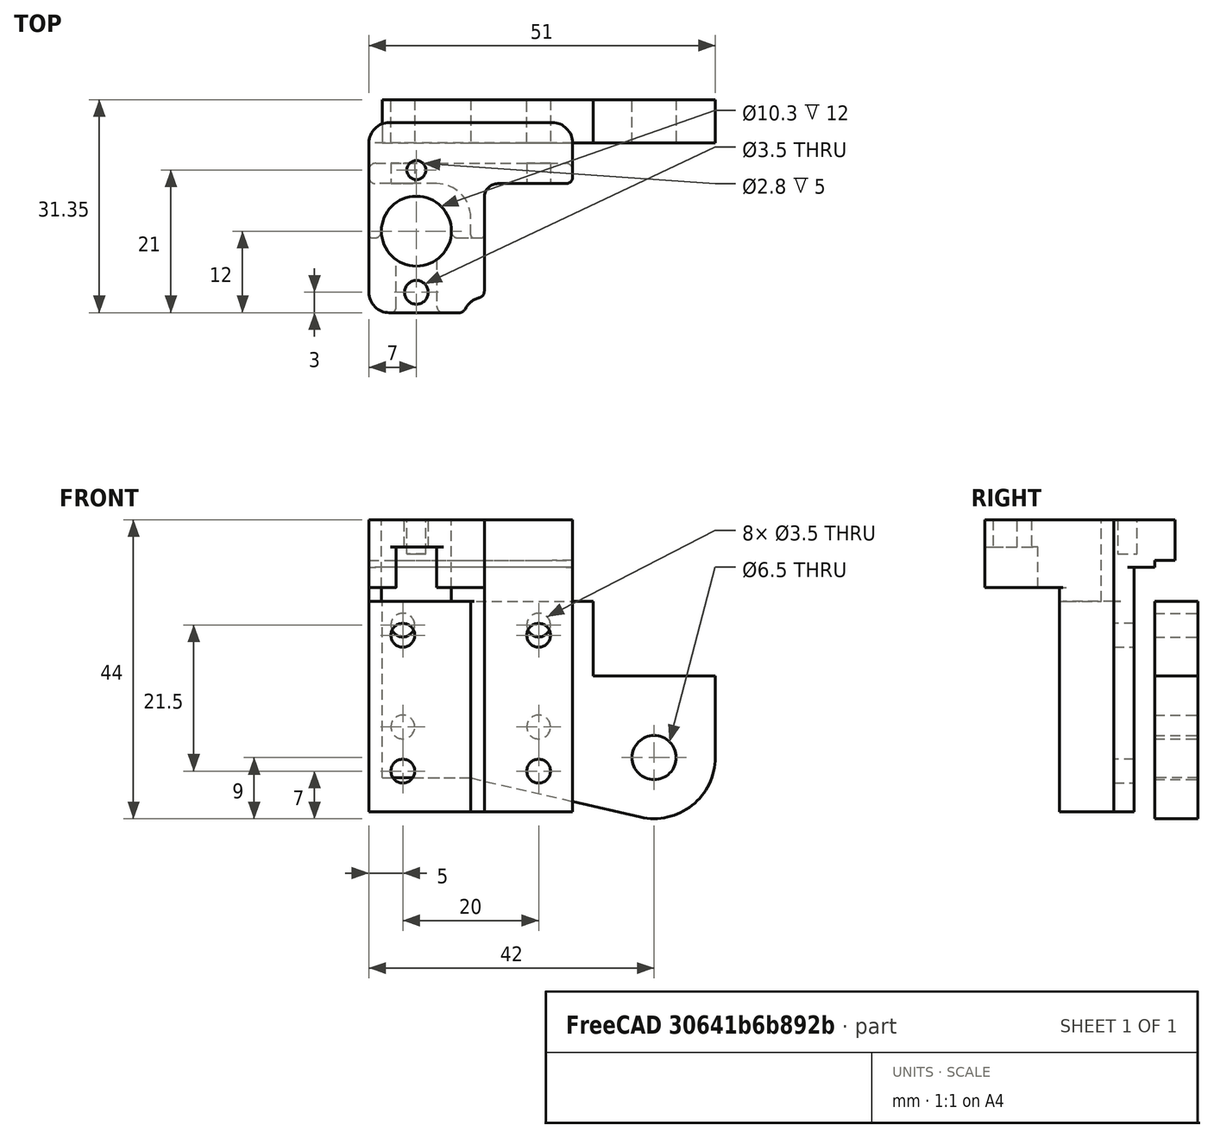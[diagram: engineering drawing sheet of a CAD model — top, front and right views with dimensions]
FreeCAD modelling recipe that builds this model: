
FCSTD DOCUMENT  (FreeCAD 0.19R)
Label: ZnutHolder_H5
License: All rights reserved
LicenseURL: http://en.wikipedia.org/wiki/All_rights_reserved
objects: PartDesign::Fillet×14, Sketcher::SketchObject×10, PartDesign::Pocket×8, PartDesign::Pad×2, PartDesign::Body×2, Mesh::Feature×1
note: 60 computed .brp shape members not serialized (recipe doc carries the construction recipe); baked Part::Feature solids carry a one-line shape summary decoded from their .brp

FEATURE [Sketcher::SketchObject] Sketch
  FullyConstrained = false
  MapMode = 5
  Placement = pos=(0,0,0) rot=(1,0,0;1.5708rad)
  Support = -> [XZ_Plane]
  sketch-geometry (14):
    g0: Circle CenterX=-10 CenterY=7.5 CenterZ=0 NormalX=0 NormalY=0 NormalZ=1 AngleXU=0 Radius=1.75
    g1: Circle CenterX=10 CenterY=7.5 CenterZ=0 NormalX=0 NormalY=0 NormalZ=1 AngleXU=0 Radius=1.75
    g2: Circle CenterX=-10 CenterY=-7.5 CenterZ=0 NormalX=0 NormalY=0 NormalZ=1 AngleXU=0 Radius=1.75
    g3: Circle CenterX=10 CenterY=-7.5 CenterZ=0 NormalX=0 NormalY=0 NormalZ=1 AngleXU=0 Radius=1.75
    g4: LineSegment StartX=-13 StartY=11 StartZ=0 EndX=18 EndY=11 EndZ=0
    g5: LineSegment StartX=18 StartY=11 StartZ=0 EndX=18 EndY=0 EndZ=0
    g6: LineSegment StartX=18 StartY=0 StartZ=0 EndX=36 EndY=0 EndZ=0
    g7: LineSegment StartX=36 StartY=0 StartZ=0 EndX=36 EndY=-12 EndZ=0
    g8: LineSegment StartX=-13 StartY=-15 StartZ=0 EndX=-13 EndY=11 EndZ=0
    g9: LineSegment StartX=-13 StartY=-15 StartZ=0 EndX=0 EndY=-15 EndZ=0
    g10: LineSegment StartX=0 StartY=-15 StartZ=0 EndX=24.9743 EndY=-20.7691 EndZ=0
    g11: ArcOfCircle CenterX=27 CenterY=-12 CenterZ=0 NormalX=0 NormalY=0 NormalZ=1 AngleXU=0 Radius=9 StartAngle=4.48537 EndAngle=6.28319
    g12: Circle CenterX=27 CenterY=-12 CenterZ=0 NormalX=0 NormalY=0 NormalZ=1 AngleXU=0 Radius=3.25
    g13: LineSegment StartX=19 StartY=18.0628 StartZ=0 EndX=19 EndY=-24.6673 EndZ=0
  constraints (37):
    c: Symmetric(g0,g1,g-2)
    c: Symmetric(g3,g2,g-2)
    c: Symmetric(g3,g1,g-1)
    c: Diameter(g0) = 3.5
    c: Equal(g0,g1)
    c: Equal(g0,g2)
    c: Equal(g0,g3)
    c: Distance(g1,g0) = 20
    c: Distance(g3,g1) = 15
    c: Horizontal(g4)
    c: Coincident(g4,g5)
    c: Vertical(g5)
    c: Coincident(g5,g6)
    c: Horizontal(g6)
    c: Coincident(g6,g7)
    c: Vertical(g7)
    c: Vertical(g8)
    c: DistanceX(g4) = 18
    c: DistanceX(g4) = -13
    c: Coincident(g8,g9)
    c: PointOnObject(g9,g-2)
    c: Horizontal(g9)
    c: Coincident(g9,g10)
    c: Tangent(g7,g11) = 1.5708
    c: Coincident(g11,g7)
    c: Tangent(g11,g10) = -1.5708
    c: Coincident(g12,g11)
    c: Diameter(g12) = 6.5
    c: Diameter(g11) = 18
    c: Vertical(g13)
    c: DistanceX(g13) = 19
    c: Distance(g11,g13) = 8
    c: Distance(g11,g6) = 12
    c: PointOnObject(g5,g-1)
    c: Coincident(g8,g4)
    c: DistanceY(g4) = 11
    c: DistanceY(g8) = -15
FEATURE [PartDesign::Pad] Pad
  Direction = (1,1,1)
  Length = 6.35
  Length2 = 100
  Placement = pos=(0,0,0) rot=(1,0,0;1.5708rad)
  Profile = -> Sketch
  Type = 0
FEATURE [PartDesign::Body] Body  label="Tab"
  Group = -> [Sketch,Pad]
  Origin = -> Origin
  Placement = pos=(0,6.35,0) rot=(0,0,1;0rad)
  Tip = -> Pad
FEATURE [Sketcher::SketchObject] Sketch005  label="body"
  FullyConstrained = true
  MapMode = 5
  Placement = pos=(0,0,0) rot=(0.57735,0.57735,0.57735;2.0944rad)
  Support = -> [YZ_Plane001]
  sketch-geometry (8):
    g0: LineSegment StartX=0 StartY=-20 StartZ=0 EndX=0 EndY=17 EndZ=0
    g1: LineSegment StartX=0 StartY=17 StartZ=0 EndX=3 EndY=17 EndZ=0
    g2: LineSegment StartX=3 StartY=17 StartZ=0 EndX=3 EndY=23 EndZ=0
    g3: LineSegment StartX=3 StartY=23 StartZ=0 EndX=-25 EndY=23 EndZ=0
    g4: LineSegment StartX=-25 StartY=23 StartZ=0 EndX=-25 EndY=13 EndZ=0
    g5: LineSegment StartX=-25 StartY=13 StartZ=0 EndX=-14 EndY=13 EndZ=0
    g6: LineSegment StartX=-14 StartY=13 StartZ=0 EndX=-14 EndY=-20 EndZ=0
    g7: LineSegment StartX=-14 StartY=-20 StartZ=0 EndX=0 EndY=-20 EndZ=0
  constraints (24):
    c: PointOnObject(g0,g-2)
    c: PointOnObject(g0,g-2)
    c: Coincident(g0,g1)
    c: Coincident(g1,g2)
    c: Vertical(g2)
    c: Coincident(g2,g3)
    c: Horizontal(g3)
    c: Coincident(g3,g4)
    c: Vertical(g4)
    c: Coincident(g4,g5)
    c: Horizontal(g5)
    c: Coincident(g5,g6)
    c: Vertical(g6)
    c: Coincident(g6,g7)
    c: Coincident(g7,g0)
    c: Horizontal(g7)
    c: Distance(g4) = 10
    c: DistanceY(g2) = 23
    c: DistanceX(g4) = -25
    c: Distance(g7) = 14
    c: DistanceY(g0) = -20
    c: DistanceX(g2) = 3
    c: Horizontal(g1)
    c: Distance(g2) = 6
FEATURE [PartDesign::Pad] Pad001
  Direction = (1,1,1)
  Length = 15
  Length2 = 15
  Placement = pos=(0,0,0) rot=(0.57735,0.57735,0.57735;2.0944rad)
  Profile = -> Sketch005
  Type = 4
FEATURE [Sketcher::SketchObject] Sketch007  label="ScrewHoles_rail"
  FullyConstrained = true
  MapMode = 5
  Placement = pos=(-6e-15,-14,2.3e-14) rot=(0.57735,0.57735,-0.57735;2.0944rad)
  sketch-geometry (8):
    g0: Circle CenterX=-6 CenterY=10 CenterZ=0 NormalX=0 NormalY=0 NormalZ=1 AngleXU=0 Radius=1.75
    g1: Circle CenterX=14 CenterY=10 CenterZ=0 NormalX=0 NormalY=0 NormalZ=1 AngleXU=0 Radius=1.75
    g2: Circle CenterX=-6 CenterY=-10 CenterZ=0 NormalX=0 NormalY=0 NormalZ=1 AngleXU=0 Radius=1.75
    g3: Circle CenterX=14 CenterY=-10 CenterZ=0 NormalX=0 NormalY=0 NormalZ=1 AngleXU=0 Radius=1.75
    g4: LineSegment StartX=-6 StartY=10 StartZ=0 EndX=-6 EndY=-10 EndZ=0
    g5: LineSegment StartX=-6 StartY=-10 StartZ=0 EndX=14 EndY=-10 EndZ=0
    g6: LineSegment StartX=14 StartY=-10 StartZ=0 EndX=14 EndY=10 EndZ=0
    g7: LineSegment StartX=14 StartY=10 StartZ=0 EndX=-6 EndY=10 EndZ=0
  constraints (19):
    c: Diameter(g0) = 3.5
    c: Equal(g0,g1)
    c: Equal(g0,g2)
    c: Equal(g0,g3)
    c: Coincident(g4,g0)
    c: Coincident(g4,g2)
    c: Coincident(g4,g5)
    c: Coincident(g5,g3)
    c: Coincident(g5,g6)
    c: Coincident(g6,g1)
    c: Coincident(g6,g7)
    c: Coincident(g7,g4)
    c: Equal(g4,g6)
    c: Equal(g7,g5)
    c: Distance(g7) = 20
    c: Distance(g6) = 20
    c: Perpendicular(g6,g5)
    c: Symmetric(g1,g3,g-1)
    c: DistanceX(g0) = -6
FEATURE [Sketcher::SketchObject] Sketch008  label="ScrewRelief"
  FullyConstrained = false
  MapMode = 5
  Placement = pos=(2.1e-14,-1.6e-14,-20) rot=(0.707107,0.707107,0;3.14159rad)
  sketch-geometry (8):
    g0: LineSegment StartX=-14.9077 StartY=0 StartZ=0 EndX=-6 EndY=0 EndZ=0
    g1: LineSegment StartX=-6 StartY=0 StartZ=0 EndX=-6 EndY=-16 EndZ=0
    g2: LineSegment StartX=-6 StartY=-16 StartZ=0 EndX=-14.9077 EndY=-16 EndZ=0
    g3: LineSegment StartX=-14.9077 StartY=-16 StartZ=0 EndX=-14.9077 EndY=0 EndZ=0
    g4: LineSegment StartX=-15.43 StartY=17.5817 StartZ=0 EndX=-6 EndY=17.5817 EndZ=0
    g5: LineSegment StartX=-6 StartY=17.5817 StartZ=0 EndX=-6 EndY=4.16376 EndZ=0
    g6: LineSegment StartX=-6 StartY=4.16376 StartZ=0 EndX=-15.43 EndY=4.16376 EndZ=0
    g7: LineSegment StartX=-15.43 StartY=4.16376 StartZ=0 EndX=-15.43 EndY=17.5817 EndZ=0
  constraints (20):
    c: Coincident(g0,g1)
    c: Coincident(g1,g2)
    c: Coincident(g2,g3)
    c: Coincident(g3,g0)
    c: Horizontal(g0)
    c: Horizontal(g2)
    c: Vertical(g1)
    c: Vertical(g3)
    c: Distance(g1) = 16
    c: DistanceY(g0) = 0
    c: DistanceX(g1) = -6
    c: Coincident(g4,g5)
    c: Coincident(g5,g6)
    c: Coincident(g6,g7)
    c: Coincident(g7,g4)
    c: Horizontal(g4)
    c: Horizontal(g6)
    c: Vertical(g5)
    c: Vertical(g7)
    c: DistanceX(g4) = -6
FEATURE [Sketcher::SketchObject] Sketch012  label="NutHole"
  FullyConstrained = true
  MapMode = 5
  Placement = pos=(-6.4e-15,1.01e-14,23) rot=(0,0,-1;1.5708rad)
  Support = -> [Pad001]
  sketch-geometry (1):
    g0: Circle CenterX=13 CenterY=-8 CenterZ=0 NormalX=0 NormalY=0 NormalZ=1 AngleXU=0 Radius=5.15
  constraints (3):
    c: Diameter(g0) = 10.3
    c: DistanceY(g0) = -8
    c: DistanceX(g0) = 13
FEATURE [Sketcher::SketchObject] Sketch013  label="Nutscrews"
  FullyConstrained = true
  MapMode = 5
  Placement = pos=(-7.2e-14,3.9e-14,35) rot=(0,0,-1;1.5708rad)
  sketch-geometry (2):
    g0: Circle CenterX=4 CenterY=-8 CenterZ=0 NormalX=0 NormalY=0 NormalZ=1 AngleXU=0 Radius=1.4
    g1: Circle CenterX=22 CenterY=-8 CenterZ=0 NormalX=0 NormalY=0 NormalZ=1 AngleXU=0 Radius=1.75
  constraints (6):
    c: DistanceY(g1) = -8
    c: DistanceY(g0) = -8
    c: DistanceX(g1) = 22
    c: DistanceX(g0) = 4
    c: Diameter(g1) = 3.5
    c: Diameter(g0) = 2.8
FEATURE [Sketcher::SketchObject] Sketch014  label="tunnel"
  ExternalGeometry = -> [Pad001]
  FullyConstrained = true
  MapMode = 5
  Placement = pos=(-1.1e-14,-25,5.5e-15) rot=(-0.57735,-0.57735,0.57735;4.18879rad)
  Support = -> [Pad001]
  sketch-geometry (4):
    g0: LineSegment StartX=-19 StartY=-5 StartZ=0 EndX=-11 EndY=-5 EndZ=0
    g1: LineSegment StartX=-11 StartY=-5 StartZ=0 EndX=-11 EndY=-11 EndZ=0
    g2: LineSegment StartX=-11 StartY=-11 StartZ=0 EndX=-19 EndY=-11 EndZ=0
    g3: LineSegment StartX=-19 StartY=-11 StartZ=0 EndX=-19 EndY=-5 EndZ=0
  constraints (12):
    c: Coincident(g0,g1)
    c: Coincident(g1,g2)
    c: Coincident(g2,g3)
    c: Coincident(g3,g0)
    c: Horizontal(g0)
    c: Horizontal(g2)
    c: Vertical(g1)
    c: Vertical(g3)
    c: Distance(g1) = 6
    c: DistanceY(g0) = -5
    c: Distance(g0) = 8
    c: Distance(g0,g-3) = 4
FEATURE [PartDesign::Pocket] Pocket
  BaseFeature = -> Pad001
  Length = 11
  Length2 = 100
  Placement = pos=(0,0,0) rot=(0.57735,0.57735,0.57735;2.0944rad)
  Profile = -> Sketch014
  Type = 0
FEATURE [Sketcher::SketchObject] Sketch015  label="backpocket"
  FullyConstrained = true
  MapMode = 5
  Placement = pos=(0,-8e-15,0) rot=(0.57735,0.57735,0.57735;4.18879rad)
  sketch-geometry (4):
    g0: LineSegment StartX=-34.47 StartY=20 StartZ=0 EndX=16 EndY=20 EndZ=0
    g1: LineSegment StartX=16 StartY=20 StartZ=0 EndX=16 EndY=-20 EndZ=0
    g2: LineSegment StartX=16 StartY=-20 StartZ=0 EndX=-34.47 EndY=-20 EndZ=0
    g3: LineSegment StartX=-34.47 StartY=-20 StartZ=0 EndX=-34.47 EndY=20 EndZ=0
  constraints (11):
    c: Coincident(g0,g1)
    c: Coincident(g1,g2)
    c: Coincident(g2,g3)
    c: Coincident(g3,g0)
    c: Horizontal(g0)
    c: Horizontal(g2)
    c: Vertical(g1)
    c: Distance(g3) = 40
    c: Symmetric(g2,g0,g-1)
    c: Distance(g0) = 50.47
    c: DistanceX(g0) = 16
FEATURE [Sketcher::SketchObject] Sketch018  label="Seamnotch"
  FullyConstrained = false
  MapMode = 5
  Placement = pos=(-1e-14,3.5e-14,35) rot=(0,0,-1;1.5708rad)
  sketch-geometry (1):
    g0: Circle CenterX=25.7356 CenterY=1.90921 CenterZ=0 NormalX=0 NormalY=0 NormalZ=1 AngleXU=0 Radius=3
  constraints (1):
    c: Diameter(g0) = 6
FEATURE [PartDesign::Pocket] Pocket001
  BaseFeature = -> Pocket
  Length = 17
  Length2 = 100
  Placement = pos=(0,0,0) rot=(0.57735,0.57735,0.57735;2.0944rad)
  Profile = -> Sketch013
  Type = 0
FEATURE [PartDesign::Pocket] Pocket002
  BaseFeature = -> Pocket001
  Length = 15
  Length2 = 100
  Placement = pos=(0,0,0) rot=(0.57735,0.57735,0.57735;2.0944rad)
  Profile = -> Sketch012
  Type = 1
FEATURE [PartDesign::Pocket] Pocket003
  BaseFeature = -> Pocket002
  Length = 5
  Length2 = 100
  Placement = pos=(0,0,0) rot=(0.57735,0.57735,0.57735;2.0944rad)
  Profile = -> Sketch007
  Type = 1
FEATURE [Sketcher::SketchObject] Sketch021  label="beltnotch"
  FullyConstrained = false
  MapMode = 5
  Placement = pos=(-6.4e-15,2.54e-14,23) rot=(0,0,-1;1.5708rad)
  sketch-geometry (4):
    g0: LineSegment StartX=6 StartY=20.1062 StartZ=0 EndX=28.1571 EndY=20.1062 EndZ=0
    g1: LineSegment StartX=28.1571 StartY=20.1062 StartZ=0 EndX=28.1571 EndY=2 EndZ=0
    g2: LineSegment StartX=28.1571 StartY=2 StartZ=0 EndX=6 EndY=2 EndZ=0
    g3: LineSegment StartX=6 StartY=2 StartZ=0 EndX=6 EndY=20.1062 EndZ=0
  constraints (10):
    c: Coincident(g0,g1)
    c: Coincident(g1,g2)
    c: Coincident(g2,g3)
    c: Coincident(g3,g0)
    c: Horizontal(g0)
    c: Horizontal(g2)
    c: Vertical(g1)
    c: Vertical(g3)
    c: DistanceX(g2) = 6
    c: DistanceY(g2) = 2
FEATURE [PartDesign::Pocket] Pocket004
  BaseFeature = -> Pocket003
  Length = 31
  Length2 = 100
  Placement = pos=(0,0,0) rot=(0.57735,0.57735,0.57735;2.0944rad)
  Profile = -> Sketch008
  Type = 0
FEATURE [PartDesign::Pocket] Pocket005
  BaseFeature = -> Pocket004
  Length = 8
  Length2 = 100
  Placement = pos=(0,0,0) rot=(0.57735,0.57735,0.57735;2.0944rad)
  Profile = -> Sketch018
  Type = 1
FEATURE [PartDesign::Pocket] Pocket006
  BaseFeature = -> Pocket005
  Length = 44
  Length2 = 100
  Placement = pos=(0,0,0) rot=(0.57735,0.57735,0.57735;2.0944rad)
  Profile = -> Sketch021
  Type = 0
FEATURE [PartDesign::Pocket] Pocket007
  BaseFeature = -> Pocket006
  Length = 3
  Length2 = 100
  Placement = pos=(0,0,0) rot=(0.57735,0.57735,0.57735;2.0944rad)
  Profile = -> Sketch015
  Type = 0
FEATURE [PartDesign::Fillet] Fillet
  Base = -> Pocket007 [Edge11,Edge9,Edge20]
  BaseFeature = -> Pocket007
  Placement = pos=(0,0,0) rot=(0.57735,0.57735,0.57735;2.0944rad)
  Radius = 3
  SupportTransform = false
FEATURE [PartDesign::Fillet] Fillet001
  Base = -> Fillet [Edge78]
  BaseFeature = -> Fillet
  Placement = pos=(0,0,0) rot=(0.57735,0.57735,0.57735;2.0944rad)
  Radius = 1
  SupportTransform = false
FEATURE [PartDesign::Fillet] Fillet002
  Base = -> Fillet001 [Edge26]
  BaseFeature = -> Fillet001
  Placement = pos=(0,0,0) rot=(0.57735,0.57735,0.57735;2.0944rad)
  Radius = 2
  SupportTransform = false
FEATURE [PartDesign::Fillet] Fillet003
  Base = -> Fillet002 [Edge25,Edge35]
  BaseFeature = -> Fillet002
  Placement = pos=(0,0,0) rot=(0.57735,0.57735,0.57735;2.0944rad)
  Radius = 1
  SupportTransform = false
FEATURE [PartDesign::Fillet] Fillet004
  Base = -> Fillet003 [Edge57]
  BaseFeature = -> Fillet003
  Placement = pos=(0,0,0) rot=(0.57735,0.57735,0.57735;2.0944rad)
  Radius = 1
  SupportTransform = false
FEATURE [PartDesign::Fillet] Fillet005
  Base = -> Fillet004 [Edge3]
  BaseFeature = -> Fillet004
  Placement = pos=(0,0,0) rot=(0.57735,0.57735,0.57735;2.0944rad)
  Radius = 1
  SupportTransform = false
FEATURE [PartDesign::Fillet] Fillet006
  Base = -> Fillet005 [Edge65]
  BaseFeature = -> Fillet005
  Placement = pos=(0,0,0) rot=(0.57735,0.57735,0.57735;2.0944rad)
  Radius = 1
  SupportTransform = false
FEATURE [PartDesign::Fillet] Fillet007
  Base = -> Fillet006 [Edge52]
  BaseFeature = -> Fillet006
  Placement = pos=(0,0,0) rot=(0.57735,0.57735,0.57735;2.0944rad)
  Radius = 5
  SupportTransform = false
FEATURE [PartDesign::Fillet] Fillet008
  Base = -> Fillet007 [Edge118]
  BaseFeature = -> Fillet007
  Placement = pos=(0,0,0) rot=(0.57735,0.57735,0.57735;2.0944rad)
  Radius = 1
  SupportTransform = false
FEATURE [PartDesign::Fillet] Fillet009
  Base = -> Fillet008 [Edge29]
  BaseFeature = -> Fillet008
  Placement = pos=(0,0,0) rot=(0.57735,0.57735,0.57735;2.0944rad)
  Radius = 0.8
  SupportTransform = false
FEATURE [PartDesign::Fillet] Fillet010
  Base = -> Fillet009 [Edge99]
  BaseFeature = -> Fillet009
  Placement = pos=(0,0,0) rot=(0.57735,0.57735,0.57735;2.0944rad)
  Radius = 0.5
  SupportTransform = false
FEATURE [PartDesign::Fillet] Fillet011
  Base = -> Fillet010 [Edge3]
  BaseFeature = -> Fillet010
  Placement = pos=(0,0,0) rot=(0.57735,0.57735,0.57735;2.0944rad)
  Radius = 0.5
  SupportTransform = false
FEATURE [PartDesign::Fillet] Fillet012
  Base = -> Fillet011 [Edge77]
  BaseFeature = -> Fillet011
  Placement = pos=(0,0,0) rot=(0.57735,0.57735,0.57735;2.0944rad)
  Radius = 0.5
  SupportTransform = false
FEATURE [PartDesign::Fillet] Fillet013
  Base = -> Fillet012 [Edge14,Edge23]
  BaseFeature = -> Fillet012
  Placement = pos=(0,0,0) rot=(0.57735,0.57735,0.57735;2.0944rad)
  Radius = 1
  SupportTransform = false
FEATURE [PartDesign::Body] Body001  label="LeadScrewMount"
  Group = -> [Sketch005,Pad001,Sketch007,Sketch008,Sketch012,Sketch013,Sketch014,Pocket,Sketch015,Sketch018,Pocket001,Pocket002,Pocket003,Pocket004,Sketch021,Pocket005,Pocket006,Pocket007,Fillet,Fillet001,Fillet002,Fillet003,Fillet004,Fillet005,Fillet006,Fillet007,Fillet008,Fillet009,Fillet010,Fillet011,Fillet012,Fillet013]
  Origin = -> Origin001
  Tip = -> Fillet013
FEATURE [Mesh::Feature] Mesh  label="Fillet013 (Meshed)"
